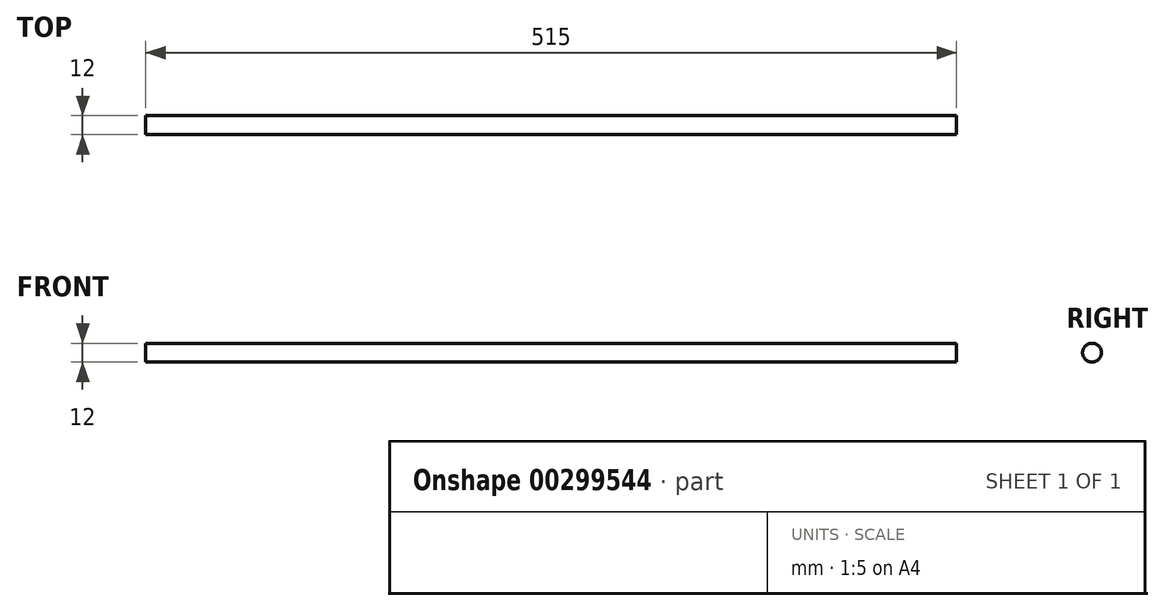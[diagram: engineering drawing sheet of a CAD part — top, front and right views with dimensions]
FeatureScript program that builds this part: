
annotation { "Feature Type Name" : "Feature", "Feature Type Description" : "" }
export const myFeature = defineFeature(function(context is Context, id is Id, definition is map)
    precondition{}
    {
        {
            var Q0;
            Q0=qCreatedBy(makeId("Right.planeOp"),FACE);
            var sketch = newSketch(context, id + "F0", { "sketchPlane" : qUnion([Q0])});
            skCircle(sketch, "E0", {"center": v(0, 0) * mm, "radius": 6 * mm});
            skSolve(sketch);
        }
        {
            var Q0;
            Q0 = qSketchRegion(id + "F0", true);
            extrude(context, id + "F1", {"entities" : qUnion([Q0]), "endBound" : BoundingType.SYMMETRIC, "depth" : 515 * mm});
        }
    });
